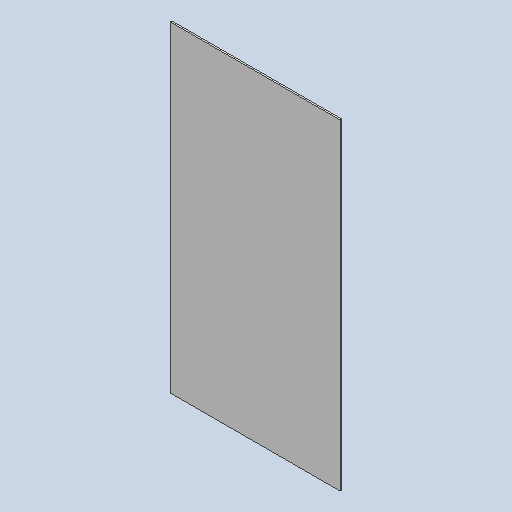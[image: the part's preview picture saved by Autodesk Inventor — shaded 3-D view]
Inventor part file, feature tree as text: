
AUTODESK INVENTOR PART (.ipt)
format: ipt  version: 2023 (Build 270158000, 158)  size: 125,440 bytes
history: native  units: in
note: dims shown in document units (in); Inventor stores cm internally (conversion verified against a paired STEP export)
features: other x3, reference x2, extrude x1, sketch x1
ambient origin geometry x8: Origin, YZ Plane, XZ Plane, XY Plane, X Axis, Y Axis, Z Axis, Center Point
bodies: Body1 (feature_tree)
feature tree (7):
  other  "Bryła1"
  extrude  "Wyciągnięcie proste1"  Depth=0.0197in TaperAngle=0.0deg
  sketch  "Szkic1"
  reference  "Odniesienie1"
  reference  "Odniesienie2"
  other  "SCIANA_2.0:1"
  other  "SCIANA_2.0_MIR:1"
